# Revit family: Shower-Slidebar-KALLISTA-TRADITIONAL-P24299
name_source: partatom
category: Specialty Equipment
units: mm (PartAtom-declared; Revit-internal decimal feet)

## family parameters
Cut with Voids When Loaded = No
Host = Face
Maintain Annotation Orientation = No
OmniClass Number = 23.31.25.00
OmniClass Title = Toilet and Bath Specialties
Part Type = Normal
Room Calculation Point = No
Round Connector Dimension = Use Diameter
Shared = No

## types (6) — shared parameters
ADA Compliant = Yes
Assembly Code = C1030200
Date Modified = 01/09/2023
Default Elevation = 42"
Description = SLIDEBAR WITH CROSS HANDLE
Height = 30"
Length = 3 7/8"
Manufacturer = Kallista Co.
Master Format 2014 = 10 28 00
Master Format 2014 Name = Toilet, Bath, and Laundry Accessories
Material = Premium Metal Construction
Product Documentation Link = https://resources.kohler.com
Product Name = Traditional
URL = http://www.kallista.com
WaterSense Certified = No
Width = 4 3/4"

## per-type parameters (varying)
| type | Finish | Model | Product Page URL | Type |
| AF-French Gold | Kallista-Metal-AF-French_Gold | P24299-00-AF |  | 1 |
| BAF-Brushed French Gold | Kallista-Metal-BAF-Brushed_French_Gold | P24299-00-BAF | https://www.kallista.com | 2 |
| BV-Brushed Bronze | Kallista-Metal-BV-Brushed_Bronze | P24299-00-BV | https://www.kallista.com | 3 |
| CP-Chrome | Kallista-Metal-CP-Chrome | P24299-00-CP | https://www.kallista.com | 4 |
| SN-Polished Nickel | Kallista-Metal-SN-Polished_Nickel | P24299-00-SN | https://www.kallista.com | 5 |
| ULB-Unlaquered Brass | Kallista-Metal-ULB-Unlaquered_Brass | P24299-00-ULB | https://www.kallista.com | 6 |

## geometry (parser evidence)
native form markers: Sweep x5
no freeform markers — native parametric forms only
